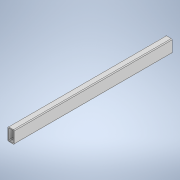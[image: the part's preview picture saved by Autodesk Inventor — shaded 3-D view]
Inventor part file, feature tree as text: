
AUTODESK INVENTOR PART (.ipt)
format: ipt  version: 2020 (Build 240168000, 168)  size: 124,928 bytes
history: native  units: in
note: dims shown in document units (in); Inventor stores cm internally (conversion verified against a paired STEP export)
features: extrude x1, sketch x1
ambient origin geometry x8: Origin, YZ Plane, XZ Plane, XY Plane, X Axis, Y Axis, Z Axis, Center Point
bodies: Solid1 (feature_tree)
feature tree (2):
  extrude  "Extrusion1"  Depth=1.0in
  sketch  "Sketch1"  dims[d0=2.0in d1=1.0in d2=0.125in d3=0.125in d4=0.125in d5=0.125in d6=0.125in d7=0.125in d8=0.125in d9=0.125in d10=0.125in d11=25.0in d12=0.0in]
